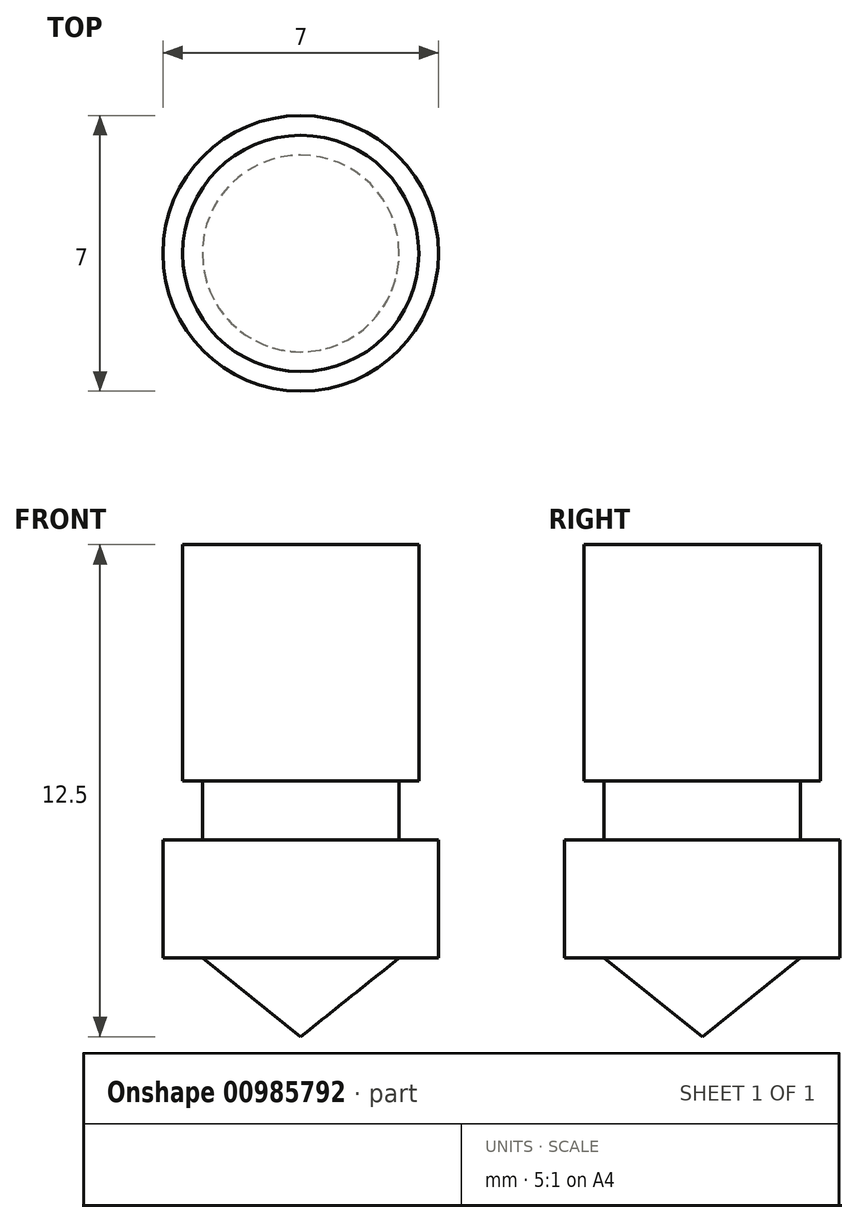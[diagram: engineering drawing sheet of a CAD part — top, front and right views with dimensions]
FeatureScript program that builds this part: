
annotation { "Feature Type Name" : "Feature", "Feature Type Description" : "" }
export const myFeature = defineFeature(function(context is Context, id is Id, definition is map)
    precondition{}
    {
        {
            var Q0;
            Q0=qCreatedBy(makeId("Front.planeOp"),FACE);
            var sketch = newSketch(context, id + "F0", { "sketchPlane" : qUnion([Q0])});
            skLineSegment(sketch, "E0", {"start": v(0, 0) * mm, "end": v(0, 63.12) * mm});
            skLineSegment(sketch, "E1", {"start": v(3.5, 2) * mm, "end": v(3.5, 5) * mm});
            skLineSegment(sketch, "E2", {"start": v(3.5, 5) * mm, "end": v(2.5, 5) * mm});
            skLineSegment(sketch, "E3", {"start": v(2.5, 5) * mm, "end": v(2.5, 6.5) * mm});
            skLineSegment(sketch, "E4", {"start": v(2.5, 6.5) * mm, "end": v(3, 6.5) * mm});
            skLineSegment(sketch, "E5", {"start": v(3, 6.5) * mm, "end": v(3, 12.5) * mm});
            skLineSegment(sketch, "E6", {"start": v(3, 12.5) * mm, "end": v(0, 12.5) * mm});
            skLineSegment(sketch, "E7", {"start": v(3.5, 2) * mm, "end": v(2.5, 2) * mm});
            skLineSegment(sketch, "E8", {"start": v(2.5, 2) * mm, "end": v(0, 0) * mm});
            skSolve(sketch);
        }
        {
            var Q0;
            Q0=makeQuery(id+"F0.imprint","IMPRINT",FACE,{"disambiguationData":[TD([[makeQuery(id+"F0.imprint","IMPRINT",EDGE,{"derivedFrom":sQuery(id+"F0.wireOp",EDGE,"E1")}),1.0]])]});
            var Q1;
            Q1=sQuery(id+"F0.wireOp",EDGE,"E0");
            revolve(context, id + "F1", {"surfaceOperationType" : NewSurfaceOperationType.ADD, "entities" : qUnion([Q0]), "axis" : qUnion([Q1]), "revolveType" : RevolveType.FULL});
        }
    });
